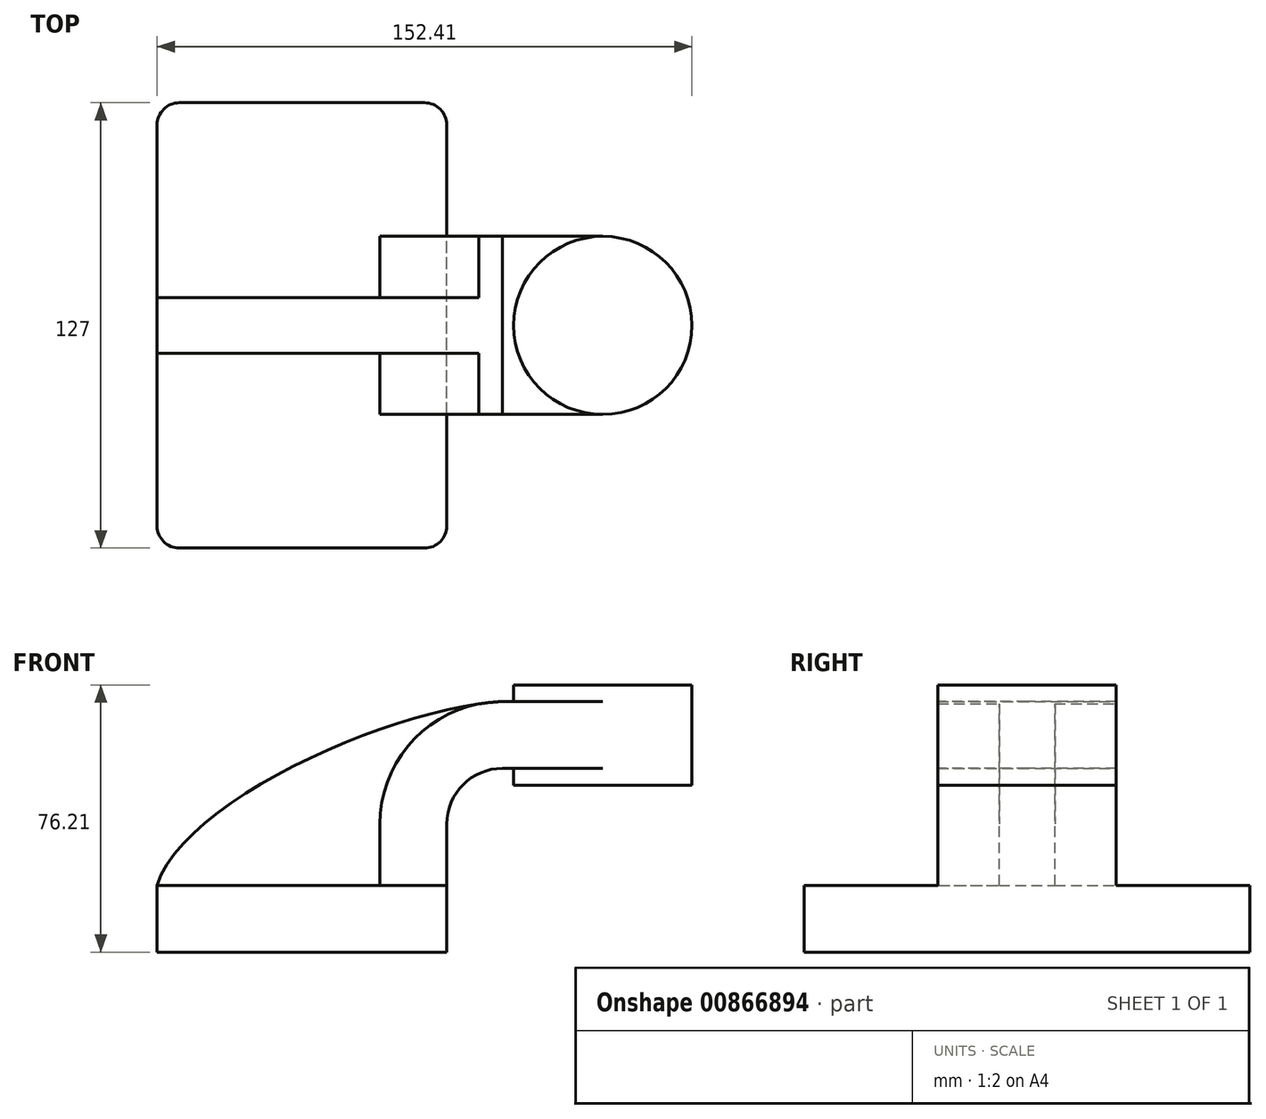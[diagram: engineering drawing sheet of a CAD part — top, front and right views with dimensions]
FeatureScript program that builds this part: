
annotation { "Feature Type Name" : "Feature", "Feature Type Description" : "" }
export const myFeature = defineFeature(function(context is Context, id is Id, definition is map)
    precondition{}
    {
        {
            var Q0;
            Q0=qCreatedBy(makeId("Front.planeOp"),FACE);
            var sketch = newSketch(context, id + "F0", { "sketchPlane" : qUnion([Q0])});
            skLineSegment(sketch, "E0.bottom", {"start": v(41.28, -9.52) * mm, "end": v(-41.28, -9.52) * mm});
            skLineSegment(sketch, "E0.top", {"start": v(41.28, 9.53) * mm, "end": v(-41.28, 9.53) * mm});
            skLineSegment(sketch, "E0.left", {"start": v(41.28, -9.52) * mm, "end": v(41.28, 9.53) * mm});
            skLineSegment(sketch, "E0.right", {"start": v(-41.28, -9.52) * mm, "end": v(-41.28, 9.53) * mm});
            skPoint(sketch, "E0.middle", {"position": v(0, 0) * mm});
            skLineSegment(sketch, "E1", {"start": v(41.28, 9.53) * mm, "end": v(41.28, 27) * mm});
            skArc(sketch, "E2", {"start": v(41.27, 27) * mm, "mid": v(45.92, 38.23) * mm, "end": v(57.15, 42.88) * mm});
            skLineSegment(sketch, "E3.bottom", {"start": v(111.13, 38.1) * mm, "end": v(60.33, 38.1) * mm});
            skLineSegment(sketch, "E3.top", {"start": v(111.13, 66.68) * mm, "end": v(60.33, 66.68) * mm});
            skLineSegment(sketch, "E3.left", {"start": v(111.13, 38.1) * mm, "end": v(111.13, 66.68) * mm});
            skLineSegment(sketch, "E3.right", {"start": v(60.33, 38.1) * mm, "end": v(60.33, 66.68) * mm});
            skPoint(sketch, "E3.middle", {"position": v(85.73, 52.39) * mm});
            skLineSegment(sketch, "E4", {"start": v(57.15, 42.88) * mm, "end": v(85.73, 42.88) * mm});
            skLineSegment(sketch, "E5.0", {"start": v(57.15, 61.93) * mm, "end": v(85.73, 61.93) * mm});
            skArc(sketch, "E5.1", {"start": v(22.23, 27) * mm, "mid": v(32.45, 51.7) * mm, "end": v(57.15, 61.93) * mm});
            skLineSegment(sketch, "E5.2", {"start": v(22.22, 9.53) * mm, "end": v(22.22, 27) * mm});
            skLineSegment(sketch, "E6", {"start": v(85.73, 38.1) * mm, "end": v(85.73, 66.68) * mm});
            skFitSpline(sketch, "E7", {"points": [v(-41.28, 9.52) * mm, v(57.15, 61.93) * mm], "startDerivative": vector(22.37, 73.33) * mm, "endDerivative": vector(91.52, 4.44) * mm});
            skSolve(sketch);
        }
        {
            var Q0;
            Q0=makeQuery(id+"F0.imprint","IMPRINT",FACE,{"disambiguationData":[TD([[makeQuery(id+"F0.imprint","IMPRINT",EDGE,{"derivedFrom":sQuery(id+"F0.wireOp",EDGE,"E0.bottom")}),-1.0]])]});
            extrude(context, id + "F1", {"entities" : qUnion([Q0]), "endBound" : BoundingType.SYMMETRIC, "depth" : 127 * mm, "offsetDistance" : 25.4 * mm});
        }
        {
            var Q0;
            {var subQ5=sQuery(id+"F0.wireOp",EDGE,"E1");Q0=makeQuery(id+"F0.imprint","IMPRINT",FACE,{"disambiguationData":[TD([[makeQuery(id+"F0.imprint","IMPRINT",EDGE,{"derivedFrom":subQ5}),1.0]])]});}
            var Q1;
            {var subQ0=sQuery(id+"F0.wireOp",EDGE,"E4");var subQ1=sQuery(id+"F0.wireOp",EDGE,"E3.right");var subQ2=makeQuery(id+"F0.imprint","INTERSECT",VERTEX,{"derivedFrom":[subQ1,subQ0]});Q1=makeQuery(id+"F0.imprint","IMPRINT",FACE,{"disambiguationData":[TD([[makeQuery(id+"F0.imprint","IMPRINT",EDGE,{"disambiguationData":[TD([[subQ2,-1.0]])],"derivedFrom":subQ1}),-1.0]])]});}
            extrude(context, id + "F2", {"entities" : qUnion([Q0, Q1]), "operationType" : NewBodyOperationType.ADD, "endBound" : BoundingType.SYMMETRIC, "depth" : 50.8 * mm, "offsetDistance" : 25.4 * mm});
        }
        {
            var Q0;
            {var subQ3=sQuery(id+"F0.wireOp",EDGE,"E5.2");Q0=makeQuery(id+"F0.imprint","IMPRINT",FACE,{"disambiguationData":[TD([[makeQuery(id+"F0.imprint","IMPRINT",EDGE,{"derivedFrom":subQ3}),1.0]])]});}
            extrude(context, id + "F3", {"entities" : qUnion([Q0]), "operationType" : NewBodyOperationType.ADD, "endBound" : BoundingType.SYMMETRIC, "depth" : 15.88 * mm, "offsetDistance" : 25.4 * mm});
        }
        {
            var Q0;
            {var subQ0=sQuery(id+"F0.wireOp",EDGE,"E3.left");Q0=makeQuery(id+"F0.imprint","IMPRINT",FACE,{"disambiguationData":[TD([[makeQuery(id+"F0.imprint","IMPRINT",EDGE,{"derivedFrom":subQ0}),1.0]])]});}
            var Q1;
            Q1=sQuery(id+"F0.wireOp",EDGE,"E6");
            revolve(context, id + "F4", {"operationType" : NewBodyOperationType.ADD, "surfaceOperationType" : NewSurfaceOperationType.NEW, "entities" : qUnion([Q0]), "axis" : qUnion([Q1]), "revolveType" : RevolveType.FULL});
        }
        {
            var Q0;
            Q0=makeQuery(id+"F1.opExtrude","CAP_EDGE",EDGE,{"disambiguationData":[OSD([sQuery(id+"F0.wireOp",EDGE,"E0.left")])],"isStart":false});
            var Q1;
            Q1=makeQuery(id+"F1.opExtrude","CAP_EDGE",EDGE,{"disambiguationData":[OSD([sQuery(id+"F0.wireOp",EDGE,"E0.right")])],"isStart":false});
            var Q2;
            Q2=makeQuery(id+"F1.opExtrude","CAP_EDGE",EDGE,{"disambiguationData":[OSD([sQuery(id+"F0.wireOp",EDGE,"E0.right")])],"isStart":true});
            var Q3;
            Q3=makeQuery(id+"F1.opExtrude","CAP_EDGE",EDGE,{"disambiguationData":[OSD([sQuery(id+"F0.wireOp",EDGE,"E0.left")])],"isStart":true});
            fillet(context, id + "F5", {"entities" : qUnion([Q0, Q1, Q2, Q3]), "radius" : 6.35 * mm, "tangentPropagation" : true, "allowEdgeOverflow" : false});
        }
    });
